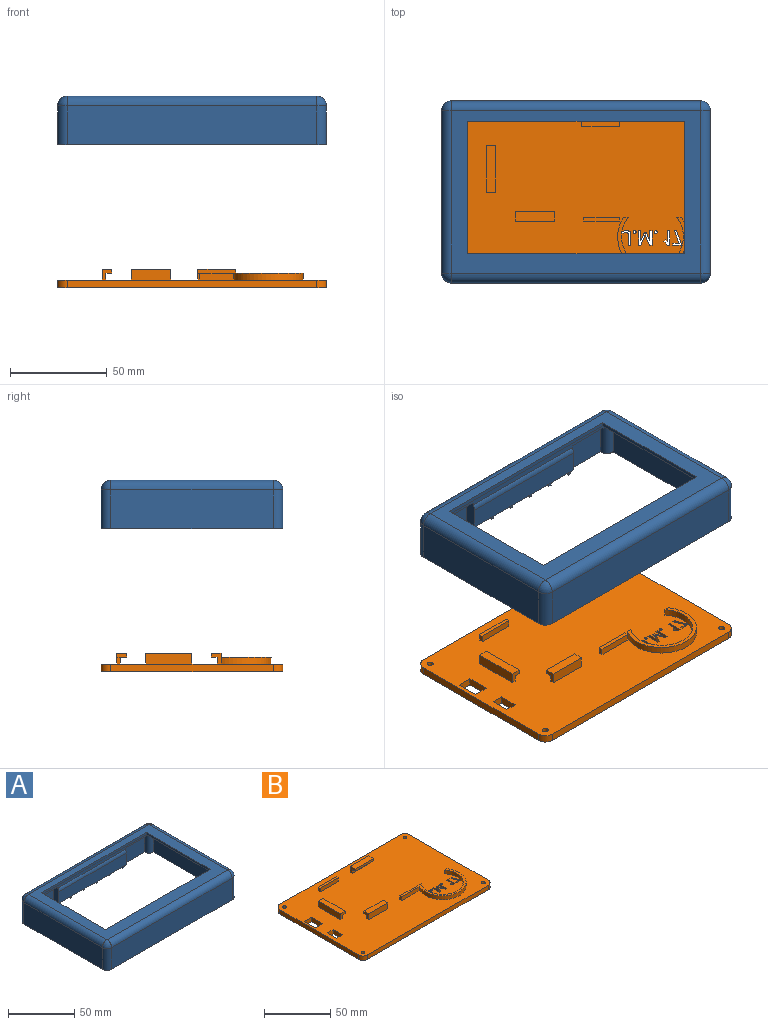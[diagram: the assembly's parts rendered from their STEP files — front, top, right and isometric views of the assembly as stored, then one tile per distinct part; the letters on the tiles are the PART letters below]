
ASSEMBLY  parts=2 mates=1
PART A: 119 faces, bbox 139x94x25 mm
  f0: plane 21x4mm, normal (0,0,-1), area 84mm2, adj f4,f109,f111,f112
  f1: plane 133x88mm, normal (0,0,-1), area 1379.3mm2, adj f2,f5,f28,f29,f40,f42,f46,f48
  f2: plane 44x19mm, normal (1,0,0), area 748.3mm2, adj f1,f6,f28,f42,f43,f110
  f3: plane 30.25x19mm, normal (0,0,-1), area 201.4mm2, adj f5,f27,f44,f48,f51,f72,f108
  f4: plane 21x19mm, normal (1,0,0), area 399mm2, adj f0,f6,f109,f111
  f5: plane 133x19mm, normal (0,-1,0), area 1544.1mm2, adj f1,f3,f6,f14,f15,f16,f17,f18
  f6: plane 139x94mm, normal (0,0,-1), area 1217.5mm2, adj f2,f4,f5,f13,f27,f28,f29,f36
  f7: plane 3.29x2mm, normal (0,-1,0), area 6.6mm2, adj f25,f65,f66,f90
  f8: plane 3.29x1.5mm, normal (0,-1,0), area 4.9mm2, adj f23,f26,f67,f90
  f9: plane 3.29x1.5mm, normal (0,-1,0), area 4.9mm2, adj f21,f24,f68,f90
  f10: plane 3.29x1.5mm, normal (0,-1,0), area 4.9mm2, adj f19,f22,f69,f90
  f11: plane 3.29x1.5mm, normal (0,-1,0), area 4.9mm2, adj f17,f20,f70,f90
  f12: plane 3.29x2mm, normal (0,-1,0), area 6.6mm2, adj f18,f71,f72,f90
  f13: plane 129x20mm, normal (0,1,0), area 2133.8mm2, adj f6,f14,f15,f16,f39,f60,f61,f62
  f14: plane 7x3mm, normal (0,0,-1), area 21mm2, adj f5,f13,f79,f82
  f15: plane 7x3mm, normal (0,0,-1), area 21mm2, adj f5,f13,f83,f84
  f16: plane 7x3mm, normal (0,0,-1), area 21mm2, adj f5,f13,f81,f85
  f17: plane 15.1x4mm, normal (-1,0,0), area 60.4mm2, adj f5,f11,f70,f77,f86
  f18: plane 15.1x4mm, normal (1,0,0), area 60.4mm2, adj f5,f12,f71,f77,f86
  f19: plane 15.1x4mm, normal (-1,0,0), area 60.4mm2, adj f5,f10,f69,f76,f87
  f20: plane 15.1x4mm, normal (1,0,0), area 60.4mm2, adj f5,f11,f70,f76,f87
  f21: plane 15.1x4mm, normal (-1,0,0), area 60.4mm2, adj f5,f9,f68,f75,f88
  f22: plane 15.1x4mm, normal (1,0,0), area 60.4mm2, adj f5,f10,f69,f75,f88
  f23: plane 15.1x4mm, normal (-1,0,0), area 60.4mm2, adj f5,f8,f67,f74,f89
  f24: plane 15.1x4mm, normal (1,0,0), area 60.4mm2, adj f5,f9,f68,f74,f89
  f25: plane 15.1x4mm, normal (-1,0,0), area 60.4mm2, adj f5,f7,f65,f73,f92
  f26: plane 15.1x4mm, normal (1,0,0), area 60.4mm2, adj f5,f8,f67,f73,f92
  f27: plane 19x19mm, normal (1,0,0), area 273.3mm2, adj f3,f5,f6,f44,f45,f108
  f28: plane 133x19mm, normal (0,1,0), area 2351.6mm2, adj f1,f2,f6,f29,f40,f41,f42,f43
  f29: plane 88x19mm, normal (-1,0,0), area 1496.6mm2, adj f1,f5,f6,f28,f40,f41,f46,f47
  f30: plane 68.5x2mm, normal (1,0,0), area 137mm2, adj f31,f33,f34,f35
  f31: plane 112x2mm, normal (0,-1,0), area 224mm2, adj f30,f32,f34,f35
  f32: plane 68.5x2mm, normal (-1,0,0), area 137mm2, adj f31,f33,f34,f35
  f33: plane 112x2mm, normal (0,1,0), area 224mm2, adj f30,f32,f34,f35
  f34: plane 129x84mm, normal (0,0,1), area 3164mm2, adj f30,f31,f32,f33,f99,f100,f104,f105
  f35: plane 122x78mm, normal (0,0,-1), area 1844mm2, adj f30,f31,f32,f33,f48,f49,f50,f51
  f36: plane 84x20mm, normal (-1,0,0), area 1680mm2, adj f6,f101,f105,f107
  f37: plane 129x20mm, normal (0,-1,0), area 2580mm2, adj f6,f96,f100,f101
  f38: plane 84x20mm, normal (1,0,0), area 1680mm2, adj f6,f96,f98,f99
  f39: plane 7x3mm, normal (0,0,-1), area 21mm2, adj f5,f13,f80,f94
  f40: cylinder r=3.5mm len=18mm, axis (0,0,1), area 175.6mm2, adj f1,f28,f29,f41
  f41: plane 5.5x5.5mm, normal (0,0,-1), area 19.7mm2, adj f28,f29,f40,f58
  f42: cylinder r=3.5mm len=18mm, axis (0,0,1), area 175.6mm2, adj f1,f2,f28,f43
  f43: plane 5.5x5.5mm, normal (0,0,-1), area 19.7mm2, adj f2,f28,f42,f56
  f44: cylinder r=3.5mm len=18mm, axis (0,0,1), area 175.6mm2, adj f3,f5,f27,f45
  f45: plane 5.5x5.5mm, normal (0,0,-1), area 19.7mm2, adj f5,f27,f44,f54
  f46: cylinder r=3.5mm len=18mm, axis (0,0,1), area 175.6mm2, adj f1,f5,f29,f47
  f47: plane 5.5x5.5mm, normal (0,0,-1), area 19.7mm2, adj f5,f29,f46,f52
  f48: plane 122x5mm, normal (0,-1,0), area 560.5mm2, adj f1,f3,f35,f49,f51,f66,f72,f93
  f49: plane 78x4mm, normal (-1,0,0), area 312mm2, adj f1,f35,f48,f50
  f50: plane 122x4mm, normal (0,1,0), area 488mm2, adj f1,f35,f49,f51
  f51: plane 78x4mm, normal (1,0,0), area 312mm2, adj f1,f3,f35,f48,f50,f114
  f52: cylinder r=1.5mm len=15mm, axis (0,0,-1), area 141.4mm2, adj f47,f53
  f53: plane 3x3mm, normal (0,0,-1), area 7.1mm2, adj f52
  f54: cylinder r=1.5mm len=15mm, axis (0,0,-1), area 141.4mm2, adj f45,f55
  f55: plane 3x3mm, normal (0,0,-1), area 7.1mm2, adj f54
  f56: cylinder r=1.5mm len=15mm, axis (0,0,-1), area 141.4mm2, adj f43,f57
  f57: plane 3x3mm, normal (0,0,-1), area 7.1mm2, adj f56
  f58: cylinder r=1.5mm len=15mm, axis (0,0,-1), area 141.4mm2, adj f41,f59
  f59: plane 3x3mm, normal (0,0,-1), area 7.1mm2, adj f58
  f60: cylinder r=3.5mm len=7mm, axis (0,1,0), area 33mm2, adj f5,f13,f84,f85
  f61: cylinder r=3.5mm len=7mm, axis (0,1,0), area 33mm2, adj f5,f13,f82,f83
  f62: cylinder r=3.5mm len=7mm, axis (0,1,0), area 33mm2, adj f5,f13,f94,f95
  f63: cylinder r=3.5mm len=7mm, axis (0,1,0), area 33mm2, adj f5,f13,f80,f81
  f64: cylinder r=3.5mm len=7mm, axis (0,1,0), area 33mm2, adj f5,f13,f78,f79
  f65: plane 4x2mm, normal (0,0,-1), area 8mm2, adj f5,f7,f25,f66
  f66: plane 18x6mm, normal (1,0,0), area 99.5mm2, adj f1,f5,f7,f48,f65,f90,f91,f93
  f67: plane 4x1.5mm, normal (0,0,-1), area 6mm2, adj f5,f8,f23,f26
  f68: plane 4x1.5mm, normal (0,0,-1), area 6mm2, adj f5,f9,f21,f24
  f69: plane 4x1.5mm, normal (0,0,-1), area 6mm2, adj f5,f10,f19,f22
  f70: plane 4x1.5mm, normal (0,0,-1), area 6mm2, adj f5,f11,f17,f20
  f71: plane 4x2mm, normal (0,0,-1), area 8mm2, adj f5,f12,f18,f72
  f72: plane 18x6mm, normal (-1,0,0), area 99.5mm2, adj f3,f5,f12,f48,f71,f90,f91,f93
  f73: plane 12.5x4mm, normal (0,0,-1), area 50mm2, adj f5,f25,f26,f92
  f74: plane 12.5x4mm, normal (0,0,-1), area 50mm2, adj f5,f23,f24,f89
  f75: plane 12.5x4mm, normal (0,0,-1), area 50mm2, adj f5,f21,f22,f88
  f76: plane 12.5x4mm, normal (0,0,-1), area 50mm2, adj f5,f19,f20,f87
  f77: plane 12.5x4mm, normal (0,0,-1), area 50mm2, adj f5,f17,f18,f86
  f78: plane 10x3mm, normal (-1,0,0), area 30mm2, adj f5,f6,f13,f64
  f79: plane 10x3mm, normal (1,0,0), area 30mm2, adj f5,f13,f14,f64
  f80: plane 10x3mm, normal (1,0,0), area 30mm2, adj f5,f13,f39,f63
  f81: plane 10x3mm, normal (-1,0,0), area 30mm2, adj f5,f13,f16,f63
  f82: plane 10x3mm, normal (-1,0,0), area 30mm2, adj f5,f13,f14,f61
  f83: plane 10x3mm, normal (1,0,0), area 30mm2, adj f5,f13,f15,f61
  f84: plane 10x3mm, normal (-1,0,0), area 30mm2, adj f5,f13,f15,f60
  f85: plane 10x3mm, normal (1,0,0), area 30mm2, adj f5,f13,f16,f60
  f86: plane 12.5x11.81mm, normal (0,1,0), area 147.6mm2, adj f17,f18,f77,f90
  f87: plane 12.5x11.81mm, normal (0,1,0), area 147.6mm2, adj f19,f20,f76,f90
  f88: plane 12.5x11.81mm, normal (0,1,0), area 147.6mm2, adj f21,f22,f75,f90
  f89: plane 12.5x11.81mm, normal (0,1,0), area 147.6mm2, adj f23,f24,f74,f90
  f90: plane 72.5x2mm, normal (0,0,-1), area 145mm2, adj f7,f8,f9,f10,f11,f12,f66,f72
  f91: plane 72.5x10.71mm, normal (0,-1,0), area 776.2mm2, adj f66,f72,f90,f93
  f92: plane 12.5x11.81mm, normal (0,1,0), area 147.6mm2, adj f25,f26,f73,f90
  f93: cylinder r=5mm len=72.5mm, axis (-1,0,0), area 233.3mm2, adj f48,f66,f72,f91
  f94: plane 10x3mm, normal (-1,0,0), area 30mm2, adj f5,f13,f39,f62
  f95: plane 10x3mm, normal (1,0,0), area 30mm2, adj f5,f6,f13,f62
  f96: cylinder r=5mm len=20mm, axis (0,0,1), area 157.1mm2, adj f6,f37,f38,f97
  f97: sphere r=5mm, area 39.3mm2, adj f96,f99,f100
  f98: cylinder r=5mm len=20mm, axis (0,0,-1), area 157.1mm2, adj f6,f13,f38,f102
  f99: cylinder r=5mm len=84mm, axis (0,1,0), area 659.7mm2, adj f34,f38,f97,f102
  f100: cylinder r=5mm len=129mm, axis (1,0,0), area 1013.2mm2, adj f34,f37,f97,f103
  f101: cylinder r=5mm len=20mm, axis (0,0,-1), area 157.1mm2, adj f6,f36,f37,f103
  f102: sphere r=5mm, area 39.3mm2, adj f98,f99,f104
  f103: sphere r=5mm, area 39.3mm2, adj f100,f101,f105
  f104: cylinder r=5mm len=129mm, axis (-1,0,0), area 1013.2mm2, adj f13,f34,f102,f106
  f105: cylinder r=5mm len=84mm, axis (0,-1,0), area 659.7mm2, adj f34,f36,f103,f106
  f106: sphere r=5mm, area 39.3mm2, adj f104,f105,f107
  f107: cylinder r=5mm len=20mm, axis (0,0,1), area 157.1mm2, adj f6,f13,f36,f106
  f108: plane 19x6mm, normal (0,1,0), area 113.6mm2, adj f3,f6,f27,f113,f114
  f109: plane 19x4mm, normal (0,-1,0), area 76mm2, adj f0,f4,f6,f112
  f110: plane 19x6mm, normal (0,-1,0), area 113.6mm2, adj f1,f2,f6,f113,f114
  f111: plane 19x4mm, normal (0,1,0), area 76mm2, adj f0,f4,f6,f112
  f112: plane 21x19mm, normal (-1,0,0), area 341.1mm2, adj f0,f6,f109,f111,f115,f116,f117,f118
  f113: plane 25x16.82mm, normal (1,0,0), area 362.6mm2, adj f6,f108,f110,f114,f115,f116,f117,f118
  f114: cylinder r=5mm len=25mm, axis (0,1,0), area 56.4mm2, adj f51,f108,f110,f113
  f115: plane 5.06x2mm, normal (0,-1,0), area 10.1mm2, adj f112,f113,f116,f118
  f116: plane 11.43x2mm, normal (0,0,-1), area 22.9mm2, adj f112,f113,f115,f117
  f117: plane 5.06x2mm, normal (0,1,0), area 10.1mm2, adj f112,f113,f116,f118
  f118: plane 11.43x2mm, normal (0,0,1), area 22.9mm2, adj f112,f113,f115,f117
PART B: 121 faces, bbox 139x94x9.5 mm
  f0: plane 20.5x5.5mm, normal (0,-1,0), area 112.8mm2, adj f9,f107,f110,f116
  f1: plane 20.5x3.5mm, normal (0,1,0), area 71.8mm2, adj f9,f107,f110,f117
  f2: plane 18.5x3.5mm, normal (0,1,0), area 64.8mm2, adj f7,f9,f26,f106
  f3: plane 19.5x3.5mm, normal (0,1,0), area 68.2mm2, adj f8,f9,f104,f109
  f4: plane 24x5.5mm, normal (-1,0,0), area 132mm2, adj f9,f105,f111,f113
  f5: plane 19.5x3.5mm, normal (0,-1,0), area 68.3mm2, adj f9,f28,f108,f118
  f6: plane 19.5x3.5mm, normal (0,-1,0), area 68.2mm2, adj f8,f9,f104,f109
  f7: plane 18.5x2mm, normal (0,0,1), area 37mm2, adj f2,f25,f26,f106
  f8: plane 19.5x2mm, normal (0,0,1), area 39mm2, adj f3,f6,f104,f109
  f9: plane 139x94mm, normal (0,0,1), area 12438.7mm2, adj f0,f1,f2,f3,f4,f5,f6,f11
  f10: plane 139x94mm, normal (0,0,-1), area 12792.3mm2, adj f13,f14,f15,f16,f17,f18,f19,f20
  f11: cylinder r=16mm len=32mm, axis (0,0,-1), area 251.5mm2, adj f9,f12,f31,f32
  f12: plane 36x28mm, normal (0,0,1), area 149.6mm2, adj f11,f30,f31,f32
  f13: plane 84x4mm, normal (1,0,0), area 336mm2, adj f9,f10,f17,f20
  f14: plane 129x4mm, normal (0,1,0), area 516mm2, adj f9,f10,f17,f18
  f15: plane 84x4mm, normal (-1,0,0), area 336mm2, adj f9,f10,f18,f19
  f16: plane 129x4mm, normal (0,-1,0), area 516mm2, adj f9,f10,f19,f20
  f17: cylinder r=5mm len=5mm, axis (0,0,1), area 31.4mm2, adj f9,f10,f13,f14
  f18: cylinder r=5mm len=5mm, axis (0,0,-1), area 31.4mm2, adj f9,f10,f14,f15
  f19: cylinder r=5mm len=5mm, axis (0,0,1), area 31.4mm2, adj f9,f10,f15,f16
  f20: cylinder r=5mm len=5mm, axis (0,0,-1), area 31.4mm2, adj f9,f10,f13,f16
  f21: cylinder r=1.5mm len=4mm, axis (0,0,1), area 37.7mm2, adj f9,f10
  f22: cylinder r=1.5mm len=4mm, axis (0,0,1), area 37.7mm2, adj f9,f10
  f23: cylinder r=1.5mm len=4mm, axis (0,0,1), area 37.7mm2, adj f9,f10
  f24: cylinder r=1.5mm len=4mm, axis (0,0,1), area 37.7mm2, adj f9,f10
  f25: plane 18.5x3.5mm, normal (0,-1,0), area 64.7mm2, adj f7,f9,f26,f106
  f26: plane 3.5x2mm, normal (1,0,0), area 7mm2, adj f2,f7,f9,f25
  f27: plane 24x3.5mm, normal (1,0,0), area 84mm2, adj f9,f105,f111,f114
  f28: plane 5.5x5.22mm, normal (1,0,0), area 17.4mm2, adj f5,f9,f29,f118,f119,f120
  f29: plane 19.5x5.5mm, normal (0,1,0), area 107.2mm2, adj f9,f28,f108,f120
  f30: cylinder r=18mm len=36mm, axis (0,0,-1), area 272.1mm2, adj f9,f12,f31,f32
  f31: plane 3.5x2.48mm, normal (0,1,0), area 8.7mm2, adj f9,f11,f12,f30
  f32: plane 3.5x2.48mm, normal (0,1,0), area 8.7mm2, adj f9,f11,f12,f30
  f33: plane 4x1.14mm, normal (0,-1,0), area 4.6mm2, adj f9,f10,f34,f38
  f34: plane 7.52x4mm, normal (-0.93,-0.36,0), area 32.3mm2, adj f9,f10,f33,f35
  f35: plane 4.72x4mm, normal (0,1,0), area 18.9mm2, adj f9,f10,f34,f36
  f36: plane 4x1mm, normal (1,0,0), area 4mm2, adj f9,f10,f35,f37
  f37: plane 4x3.27mm, normal (0,-1,0), area 13.1mm2, adj f9,f10,f36,f38
  f38: plane 6.52x4mm, normal (0.93,0.37,0), area 28.1mm2, adj f9,f10,f33,f37
  f39: plane 7.52x4mm, normal (-1,0,0), area 30.1mm2, adj f9,f10,f40,f45
  f40: plane 4x1.25mm, normal (0,1,0), area 5mm2, adj f9,f10,f39,f41
  f41: plane 4x1.91mm, normal (0.71,0.71,0), area 10.8mm2, adj f9,f10,f40,f42
  f42: plane 4x0.88mm, normal (0.71,-0.71,0), area 5mm2, adj f9,f10,f41,f43
  f43: plane 4x1.03mm, normal (-0.71,-0.71,0), area 5.8mm2, adj f9,f10,f42,f44
  f44: plane 5.76x4mm, normal (1,0,0), area 23mm2, adj f9,f10,f43,f45
  f45: plane 4x1.25mm, normal (0,-1,0), area 5mm2, adj f9,f10,f39,f44
  f46: extruded ~4x0.52mm, area 2.3mm2, adj f9,f10,f47,f53
  f47: extruded ~4x0.52mm, area 2.3mm2, adj f9,f10,f46,f48
  f48: extruded ~4x0.51mm, area 2.3mm2, adj f9,f10,f47,f49
  f49: extruded ~4x0.52mm, area 2.3mm2, adj f9,f10,f48,f50
  f50: extruded ~4x0.52mm, area 2.3mm2, adj f9,f10,f49,f51
  f51: extruded ~4x0.52mm, area 2.3mm2, adj f9,f10,f50,f52
  f52: extruded ~4x0.52mm, area 2.3mm2, adj f9,f10,f51,f53
  f53: extruded ~4x0.52mm, area 2.3mm2, adj f9,f10,f46,f52
  f54: plane 4.66x4mm, normal (0.92,0.4,0), area 20.3mm2, adj f9,f10,f55,f61
  f55: plane 4x1.87mm, normal (1,0,0), area 7.5mm2, adj f9,f10,f54,f56
  f56: plane 4x0.34mm, normal (0,-1,0), area 1.4mm2, adj f9,f10,f55,f57
  f57: plane 4.18x4mm, normal (-0.93,-0.37,0), area 18mm2, adj f9,f10,f56,f58
  f58: plane 5.17x4mm, normal (1,0,0), area 20.7mm2, adj f9,f10,f57,f59
  f59: plane 4x1.24mm, normal (0,-1,0), area 5mm2, adj f9,f10,f58,f60
  f60: plane 7.52x4mm, normal (-1,0,0), area 30.1mm2, adj f9,f10,f59,f61
  f61: plane 4x1.24mm, normal (0,1,0), area 5mm2, adj f9,f10,f54,f60
  f62: plane 7.52x4mm, normal (1,0,0), area 30.1mm2, adj f9,f10,f63,f69
  f63: plane 4x1.25mm, normal (0,-1,0), area 5mm2, adj f9,f10,f62,f64
  f64: plane 5.17x4mm, normal (-1,0,0), area 20.7mm2, adj f9,f10,f63,f65
  f65: plane 4.18x4mm, normal (0.93,-0.38,0), area 18mm2, adj f9,f10,f64,f66
  f66: plane 4x0.33mm, normal (0,-1,0), area 1.3mm2, adj f9,f10,f65,f67
  f67: plane 4x1.89mm, normal (-1,0,0), area 7.6mm2, adj f9,f10,f66,f68
  f68: plane 4.64x4mm, normal (-0.92,0.4,0), area 20.2mm2, adj f9,f10,f67,f69
  f69: plane 4x1.25mm, normal (0,1,0), area 5mm2, adj f9,f10,f62,f68
  f70: extruded ~4x0.52mm, area 2.3mm2, adj f9,f10,f71,f77
  f71: extruded ~4x0.52mm, area 2.3mm2, adj f9,f10,f70,f72
  f72: extruded ~4x0.51mm, area 2.3mm2, adj f9,f10,f71,f73
  f73: extruded ~4x0.52mm, area 2.3mm2, adj f9,f10,f72,f74
  f74: extruded ~4x0.52mm, area 2.3mm2, adj f9,f10,f73,f75
  f75: extruded ~4x0.52mm, area 2.3mm2, adj f9,f10,f74,f76
  f76: extruded ~4x0.52mm, area 2.3mm2, adj f9,f10,f75,f77
  f77: extruded ~4x0.52mm, area 2.3mm2, adj f9,f10,f70,f76
  f78: plane 4x1.24mm, normal (0,1,0), area 5mm2, adj f9,f10,f79,f95
  f79: plane 5.75x4mm, normal (1,0,0), area 23mm2, adj f9,f10,f78,f80
  f80: extruded ~4x0.71mm, area 3.3mm2, adj f9,f10,f79,f81
  f81: extruded ~4x0.86mm, area 3.6mm2, adj f9,f10,f80,f82
  f82: extruded ~4x0.46mm, area 1.8mm2, adj f9,f10,f81,f83
  f83: extruded ~4x0.47mm, area 1.9mm2, adj f9,f10,f82,f84
  f84: extruded ~4x0.41mm, area 1.7mm2, adj f9,f10,f83,f85
  f85: extruded ~4x0.29mm, area 1.3mm2, adj f9,f10,f84,f86
  f86: plane 4x0.83mm, normal (0.85,0.53,0), area 3.9mm2, adj f9,f10,f85,f87
  f87: extruded ~4x0.5mm, area 2.3mm2, adj f9,f10,f86,f88
  f88: extruded ~4x0.62mm, area 2.6mm2, adj f9,f10,f87,f89
  f89: extruded ~4x0.62mm, area 2.6mm2, adj f9,f10,f88,f90
  f90: extruded ~4x0.52mm, area 2.1mm2, adj f9,f10,f89,f91
  f91: extruded ~4x0.87mm, area 3.5mm2, adj f9,f10,f90,f92
  f92: extruded ~4x0.75mm, area 3.3mm2, adj f9,f10,f91,f93
  f93: extruded ~4x0.58mm, area 3.2mm2, adj f9,f10,f92,f94
  f94: extruded ~4x0.89mm, area 3.7mm2, adj f9,f10,f93,f95
  f95: plane 5.85x4mm, normal (-1,0,0), area 23.4mm2, adj f9,f10,f78,f94
  f96: plane 10x4mm, normal (1,0,0), area 40mm2, adj f9,f10,f97,f99
  f97: plane 6x4mm, normal (0,1,0), area 24mm2, adj f9,f10,f96,f98
  f98: plane 10x4mm, normal (-1,0,0), area 40mm2, adj f9,f10,f97,f99
  f99: plane 6x4mm, normal (0,-1,0), area 24mm2, adj f9,f10,f96,f98
  f100: plane 12x4mm, normal (-1,0,0), area 48mm2, adj f9,f10,f101,f103
  f101: plane 8x4mm, normal (0,-1,0), area 32mm2, adj f9,f10,f100,f102
  f102: plane 12x4mm, normal (1,0,0), area 48mm2, adj f9,f10,f101,f103
  f103: plane 8x4mm, normal (0,1,0), area 32mm2, adj f9,f10,f100,f102
  f104: plane 3.5x2mm, normal (-1,0,0), area 7mm2, adj f3,f6,f8,f9
  f105: plane 5.5x5mm, normal (0,1,0), area 17mm2, adj f4,f9,f27,f112,f113,f114
  f106: plane 3.5x2mm, normal (-1,0,0), area 7mm2, adj f2,f7,f9,f25
  f107: plane 5.5x5mm, normal (1,0,0), area 17mm2, adj f0,f1,f9,f115,f116,f117
  f108: plane 5.5x5.22mm, normal (-1,0,0), area 17.4mm2, adj f5,f9,f29,f118,f119,f120
  f109: plane 3.5x2mm, normal (1,0,0), area 7mm2, adj f3,f6,f8,f9
  f110: plane 5.5x5mm, normal (-1,0,0), area 17mm2, adj f0,f1,f9,f115,f116,f117
  f111: plane 5.5x5mm, normal (0,-1,0), area 17mm2, adj f4,f9,f27,f112,f113,f114
  f112: plane 24x2mm, normal (1,0,0), area 48mm2, adj f105,f111,f113,f114
  f113: plane 24x5mm, normal (0,0,1), area 120mm2, adj f4,f105,f111,f112
  f114: plane 24x3mm, normal (0,0,-1), area 72mm2, adj f27,f105,f111,f112
  f115: plane 20.5x2mm, normal (0,1,0), area 41mm2, adj f107,f110,f116,f117
  f116: plane 20.5x5mm, normal (0,0,1), area 102.5mm2, adj f0,f107,f110,f115
  f117: plane 20.5x3mm, normal (0,0,-1), area 61.5mm2, adj f1,f107,f110,f115
  f118: plane 19.5x3.22mm, normal (0,0,-1), area 62.8mm2, adj f5,f28,f108,f119
  f119: plane 19.5x2mm, normal (0,-1,0), area 39mm2, adj f28,f108,f118,f120
  f120: plane 19.5x5.22mm, normal (0,0,1), area 101.8mm2, adj f28,f29,f108,f119
PLACE A t=(-6.64,-8.88,-1.07)mm
PLACE B t=(-6.64,-8.88,-94.07)mm
MATE cylindrical B.f20 <-> A.f40  axis (0,0,1) through (57.86,-50.88,-90.07)mm
